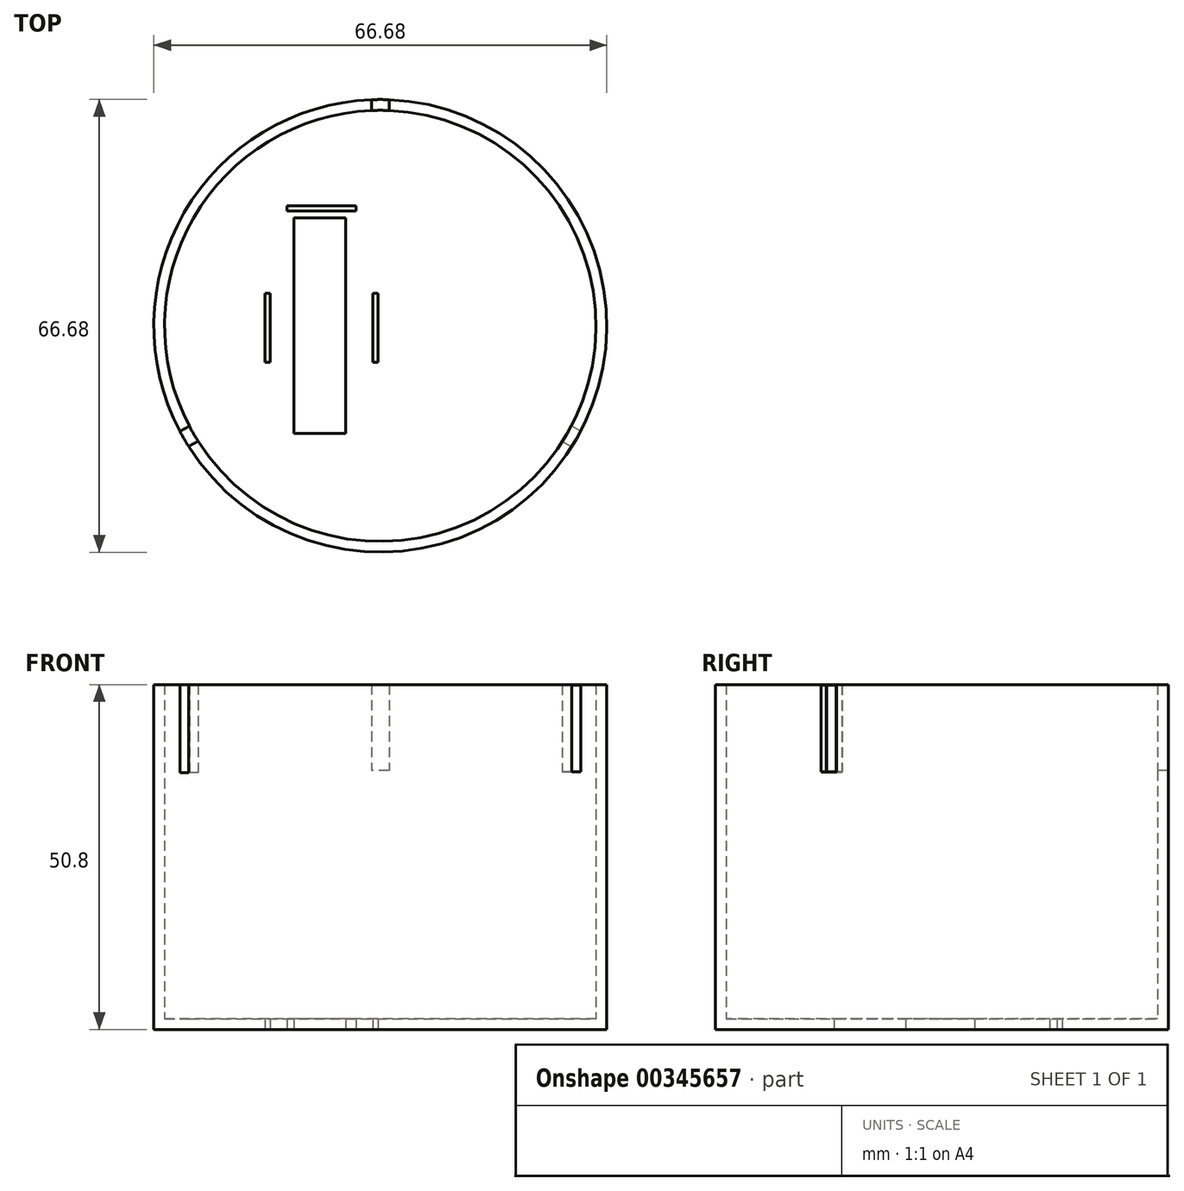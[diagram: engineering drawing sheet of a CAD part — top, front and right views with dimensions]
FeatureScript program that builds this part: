
annotation { "Feature Type Name" : "Feature", "Feature Type Description" : "" }
export const myFeature = defineFeature(function(context is Context, id is Id, definition is map)
    precondition{}
    {
        {
            var Q0;
            Q0=qCreatedBy(makeId("Top.planeOp"),FACE);
            var sketch = newSketch(context, id + "F0", { "sketchPlane" : qUnion([Q0])});
            skCircle(sketch, "E0", {"center": v(0, 0) * mm, "radius": 33.34 * mm});
            skSolve(sketch);
        }
        {
            var Q0;
            Q0=makeQuery(id+"F0.imprint","IMPRINT",FACE,{"disambiguationData":[TD([[makeQuery(id+"F0.imprint","IMPRINT",EDGE,{"derivedFrom":sQuery(id+"F0.wireOp",EDGE,"E0")}),1.0]])]});
            extrude(context, id + "F1", {"entities" : qUnion([Q0]), "depth" : 50.8 * mm});
        }
        {
            var Q0;
            Q0=makeQuery(id+"F1.opExtrude","CAP_FACE",FACE,{"disambiguationData":[OSD([sQuery(id+"F0.wireOp",EDGE,"E0")])],"isStart":false});
            shell(context, id + "F2", {"entities" : qUnion([Q0]), "thickness" : 1.59 * mm});
        }
        {
            var Q0;
            Q0=qCreatedBy(makeId("Top.planeOp"),FACE);
            var sketch = newSketch(context, id + "F3", { "sketchPlane" : qUnion([Q0])});
            skLineSegment(sketch, "E1", {"start": v(58.26, 0) * mm, "end": v(0, 0) * mm, "construction": true});
            skLineSegment(sketch, "E2", {"start": v(0, 0) * mm, "end": v(47.3, -27.3) * mm, "construction": true});
            skLineSegment(sketch, "E3", {"start": v(-50.45, 0) * mm, "end": v(0, 0) * mm, "construction": true});
            skLineSegment(sketch, "E4", {"start": v(0, 0) * mm, "end": v(-51.5, -29.73) * mm, "construction": true});
            skSolve(sketch);
        }
        {
            var Q0;
            Q0=sQuery(id+"F3.wireOp",EDGE,"E4");
            var Q1;
            Q1=sQuery(id+"F3.wireOp",VERTEX,"E4.start");
            cPlane(context, id + "F4", {"entities" : qUnion([Q0, Q1]), "cplaneType" : CPlaneType.LINE_POINT, "offset" : 25.4 * mm, "width" : 152.4 * mm, "height" : 152.4 * mm});
        }
        {
            var Q0;
            Q0=qCreatedBy(id+"F4.planeOp",FACE);
            cPlane(context, id + "F5", {"entities" : qUnion([Q0]), "cplaneType" : CPlaneType.OFFSET, "offset" : 33.34 * mm, "width" : 152.4 * mm, "height" : 152.4 * mm});
        }
        {
            var Q0;
            Q0=qCreatedBy(id+"F5.planeOp",FACE);
            var sketch = newSketch(context, id + "F6", { "sketchPlane" : qUnion([Q0])});
            skLineSegment(sketch, "E5.bottom", {"start": v(-1.27, 37.8) * mm, "end": v(1.27, 37.8) * mm});
            skLineSegment(sketch, "E5.top", {"start": v(-1.27, 51) * mm, "end": v(1.27, 51) * mm});
            skLineSegment(sketch, "E5.left", {"start": v(-1.27, 37.8) * mm, "end": v(-1.27, 51) * mm});
            skLineSegment(sketch, "E5.right", {"start": v(1.27, 37.8) * mm, "end": v(1.27, 51) * mm});
            skPoint(sketch, "E5.middle", {"position": v(0, 44.4) * mm});
            skSolve(sketch);
        }
        {
            var Q0;
            Q0=makeQuery(id+"F6.imprint","IMPRINT",FACE,{"disambiguationData":[TD([[makeQuery(id+"F6.imprint","IMPRINT",EDGE,{"derivedFrom":sQuery(id+"F6.wireOp",EDGE,"E5.bottom")}),1.0]])]});
            extrude(context, id + "F7", {"entities" : qUnion([Q0]), "operationType" : NewBodyOperationType.REMOVE, "oppositeDirection" : true, "depth" : 12.7 * mm});
        }
        {
            var Q0;
            Q0=sQuery(id+"F3.wireOp",EDGE,"E2");
            var Q1;
            Q1=sQuery(id+"F3.wireOp",VERTEX,"E4.start");
            cPlane(context, id + "F8", {"entities" : qUnion([Q0, Q1]), "cplaneType" : CPlaneType.LINE_POINT, "offset" : 25.4 * mm, "width" : 152.4 * mm, "height" : 152.4 * mm});
        }
        {
            var Q0;
            Q0=qCreatedBy(id+"F8.planeOp",FACE);
            cPlane(context, id + "F9", {"entities" : qUnion([Q0]), "cplaneType" : CPlaneType.OFFSET, "offset" : 33.27 * mm, "width" : 152.4 * mm, "height" : 152.4 * mm});
        }
        {
            var Q0;
            Q0=qCreatedBy(id+"F9.planeOp",FACE);
            var sketch = newSketch(context, id + "F10", { "sketchPlane" : qUnion([Q0])});
            skLineSegment(sketch, "E6.bottom", {"start": v(-1.34, 37.95) * mm, "end": v(1.34, 37.95) * mm});
            skLineSegment(sketch, "E6.top", {"start": v(-1.34, 50.73) * mm, "end": v(1.34, 50.73) * mm});
            skLineSegment(sketch, "E6.left", {"start": v(-1.34, 37.95) * mm, "end": v(-1.34, 50.73) * mm});
            skLineSegment(sketch, "E6.right", {"start": v(1.34, 37.95) * mm, "end": v(1.34, 50.73) * mm});
            skPoint(sketch, "E6.middle", {"position": v(0, 44.34) * mm});
            skSolve(sketch);
        }
        {
            var Q0;
            Q0=makeQuery(id+"F10.imprint","IMPRINT",FACE,{"disambiguationData":[TD([[makeQuery(id+"F10.imprint","IMPRINT",EDGE,{"derivedFrom":sQuery(id+"F10.wireOp",EDGE,"E6.bottom")}),1.0]])]});
            extrude(context, id + "F11", {"entities" : qUnion([Q0]), "operationType" : NewBodyOperationType.REMOVE, "oppositeDirection" : true, "depth" : 2.8 * mm, "hasSecondDirection" : true, "secondDirectionOppositeDirection" : false, "secondDirectionDepth" : 2.41 * mm});
        }
        {
            var Q0;
            Q0=qCreatedBy(makeId("Front.planeOp"),FACE);
            cPlane(context, id + "F12", {"entities" : qUnion([Q0]), "cplaneType" : CPlaneType.OFFSET, "offset" : 33.81 * mm, "oppositeDirection" : true, "width" : 152.4 * mm, "height" : 152.4 * mm});
        }
        {
            var Q0;
            Q0=qCreatedBy(id+"F12.planeOp",FACE);
            var sketch = newSketch(context, id + "F13", { "sketchPlane" : qUnion([Q0])});
            skLineSegment(sketch, "E7.bottom", {"start": v(1.3, 38.14) * mm, "end": v(-1.3, 38.14) * mm});
            skLineSegment(sketch, "E7.top", {"start": v(1.3, 50.9) * mm, "end": v(-1.3, 50.9) * mm});
            skLineSegment(sketch, "E7.left", {"start": v(1.3, 38.14) * mm, "end": v(1.3, 50.9) * mm});
            skLineSegment(sketch, "E7.right", {"start": v(-1.3, 38.14) * mm, "end": v(-1.3, 50.9) * mm});
            skPoint(sketch, "E7.middle", {"position": v(0, 44.52) * mm});
            skSolve(sketch);
        }
        {
            var Q0;
            Q0=makeQuery(id+"F13.imprint","IMPRINT",FACE,{"disambiguationData":[TD([[makeQuery(id+"F13.imprint","IMPRINT",EDGE,{"derivedFrom":sQuery(id+"F13.wireOp",EDGE,"E7.bottom")}),-1.0]])]});
            extrude(context, id + "F14", {"entities" : qUnion([Q0]), "operationType" : NewBodyOperationType.REMOVE, "oppositeDirection" : true, "depth" : 5.05 * mm, "hasSecondDirection" : true, "secondDirectionOppositeDirection" : false, "secondDirectionDepth" : 4.72 * mm});
        }
        {
            var Q0;
            Q0=qCreatedBy(makeId("Top.planeOp"),FACE);
            var sketch = newSketch(context, id + "F15", { "sketchPlane" : qUnion([Q0])});
            skLineSegment(sketch, "E8.bottom", {"start": v(-12.7, -15.88) * mm, "end": v(-5.08, -15.88) * mm});
            skLineSegment(sketch, "E8.top", {"start": v(-12.7, 15.88) * mm, "end": v(-5.08, 15.88) * mm});
            skLineSegment(sketch, "E8.left", {"start": v(-12.7, -15.88) * mm, "end": v(-12.7, 15.88) * mm});
            skLineSegment(sketch, "E8.right", {"start": v(-5.08, -15.88) * mm, "end": v(-5.08, 15.88) * mm});
            skLineSegment(sketch, "E9", {"start": v(0, -15.24) * mm, "end": v(20.32, -15.24) * mm, "construction": true});
            skPoint(sketch, "E10.middle", {"position": v(-6.77, 9.81) * mm});
            skPoint(sketch, "E11.middle", {"position": v(-16.64, -0.14) * mm});
            skLineSegment(sketch, "E12.left", {"start": v(-16.31, 11.35) * mm, "end": v(-16.31, 11.18) * mm});
            skLineSegment(sketch, "E12.right", {"start": v(-6.15, 11.35) * mm, "end": v(-6.15, 11.18) * mm});
            skPoint(sketch, "E13.middle", {"position": v(-16.6, -0.14) * mm});
            skPoint(sketch, "E14.middle", {"position": v(-0.72, -0.14) * mm});
            skLineSegment(sketch, "E15", {"start": v(-1.58, -15.49) * mm, "end": v(18.74, -15.49) * mm, "construction": true});
            skPoint(sketch, "E16.middle", {"position": v(-16.55, -0.23) * mm});
            skPoint(sketch, "E17.middle", {"position": v(-0.68, -0.23) * mm});
            skPoint(sketch, "E17.top.end.orphan", {"position": v(-0.28, 4.85) * mm});
            skPoint(sketch, "E17.bottom.end.orphan", {"position": v(-0.28, -5.31) * mm});
            skPoint(sketch, "E16.right.start.orphan", {"position": v(-16.15, -5.31) * mm});
            skPoint(sketch, "E16.left.start.orphan", {"position": v(-16.95, -5.31) * mm});
            skPoint(sketch, "E16.top.end.orphan", {"position": v(-16.15, 4.85) * mm});
            skPoint(sketch, "E16.top.start.orphan", {"position": v(-16.95, 4.85) * mm});
            skPoint(sketch, "E18.middle", {"position": v(-16.61, 2.5) * mm});
            skPoint(sketch, "E18.right.end.orphan", {"position": v(-16.22, 2.5) * mm});
            skPoint(sketch, "E18.left.end.orphan", {"position": v(-17, 2.5) * mm});
            skPoint(sketch, "E18.bottom.end.orphan", {"position": v(-16.22, -2.59) * mm});
            skPoint(sketch, "E18.bottom.start.orphan", {"position": v(-17, -2.59) * mm});
            skPoint(sketch, "E19.middle", {"position": v(-16.61, -0.27) * mm});
            skPoint(sketch, "E19.top.end.orphan", {"position": v(-16.22, 4.8) * mm});
            skPoint(sketch, "E19.top.start.orphan", {"position": v(-17, 4.8) * mm});
            skPoint(sketch, "E19.bottom.end.orphan", {"position": v(-16.22, -5.35) * mm});
            skPoint(sketch, "E19.bottom.start.orphan", {"position": v(-17, -5.35) * mm});
            skLineSegment(sketch, "E20.bottom", {"start": v(-16.95, -5.35) * mm, "end": v(-16.18, -5.35) * mm});
            skLineSegment(sketch, "E20.top", {"start": v(-16.95, 4.8) * mm, "end": v(-16.18, 4.8) * mm});
            skLineSegment(sketch, "E20.left", {"start": v(-16.95, -5.35) * mm, "end": v(-16.95, 4.8) * mm});
            skLineSegment(sketch, "E20.right", {"start": v(-16.18, -5.35) * mm, "end": v(-16.18, 4.8) * mm});
            skPoint(sketch, "E20.middle", {"position": v(-16.56, -0.27) * mm});
            skLineSegment(sketch, "E21.bottom", {"start": v(-1.07, -5.35) * mm, "end": v(-0.3, -5.35) * mm});
            skLineSegment(sketch, "E21.top", {"start": v(-1.07, 4.8) * mm, "end": v(-0.3, 4.8) * mm});
            skLineSegment(sketch, "E21.right", {"start": v(-0.3, -5.35) * mm, "end": v(-0.3, 4.8) * mm});
            skPoint(sketch, "E21.middle", {"position": v(-0.69, -0.27) * mm});
            skLineSegment(sketch, "E22.bottom", {"start": v(-13.74, 17.7) * mm, "end": v(-3.58, 17.7) * mm});
            skLineSegment(sketch, "E22.top", {"start": v(-13.74, 16.95) * mm, "end": v(-3.58, 16.95) * mm});
            skLineSegment(sketch, "E22.left", {"start": v(-13.74, 17.7) * mm, "end": v(-13.74, 16.95) * mm});
            skLineSegment(sketch, "E22.right", {"start": v(-3.58, 17.7) * mm, "end": v(-3.58, 16.95) * mm});
            skLineSegment(sketch, "E23", {"start": v(-1.07, -5.35) * mm, "end": v(-1.07, 4.8) * mm});
            skSolve(sketch);
        }
        {
            var Q0;
            Q0=makeQuery(id+"F15.imprint","IMPRINT",FACE,{"disambiguationData":[TD([[makeQuery(id+"F15.imprint","IMPRINT",EDGE,{"derivedFrom":sQuery(id+"F15.wireOp",EDGE,"E8.bottom")}),1.0]])]});
            var Q1;
            Q1=makeQuery(id+"F15.imprint","IMPRINT",FACE,{"disambiguationData":[TD([[makeQuery(id+"F15.imprint","IMPRINT",EDGE,{"derivedFrom":sQuery(id+"F15.wireOp",EDGE,"E21.bottom")}),1.0]])]});
            var Q2;
            Q2=makeQuery(id+"F15.imprint","IMPRINT",FACE,{"disambiguationData":[TD([[makeQuery(id+"F15.imprint","IMPRINT",EDGE,{"derivedFrom":sQuery(id+"F15.wireOp",EDGE,"E20.bottom")}),1.0]])]});
            var Q3;
            Q3=makeQuery(id+"F15.imprint","IMPRINT",FACE,{"disambiguationData":[TD([[makeQuery(id+"F15.imprint","IMPRINT",EDGE,{"derivedFrom":sQuery(id+"F15.wireOp",EDGE,"E22.bottom")}),-1.0]])]});
            extrude(context, id + "F16", {"entities" : qUnion([Q0, Q1, Q2, Q3]), "operationType" : NewBodyOperationType.REMOVE, "depth" : 9.9 * mm});
        }
    });
